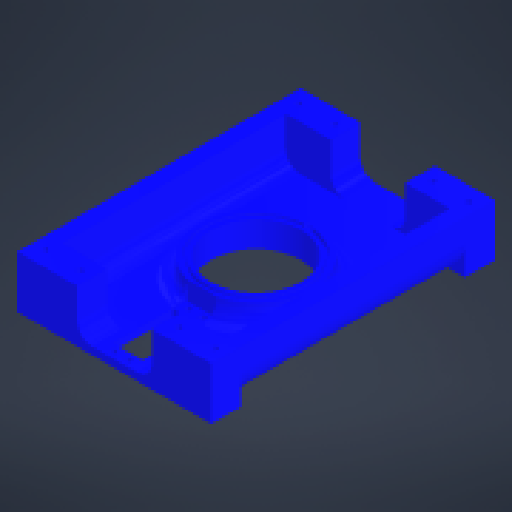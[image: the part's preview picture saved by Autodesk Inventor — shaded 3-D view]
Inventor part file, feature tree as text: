
AUTODESK INVENTOR PART (.ipt)
format: ipt  version: 2024 (Build 280153000, 153)  size: 495,616 bytes
history: native  units: mm
features: other x11, reference x9, extrude x8, sketch x8, projected_geometry x3, mirror x2, imported_body x1
ambient origin geometry x8: Origin, YZ Plane, XZ Plane, XY Plane, X Axis, Y Axis, Z Axis, Center Point
bodies: Body1 (feature_tree)
feature tree (42):
  other  "Твердое тело1"
  extrude  "Выдавливание2"  TaperAngle=0.0deg  [1 undecoded]
  other  "РабПлоскость1"
  other  "РабПлоскость2"
  mirror  "Зеркальное отражение1"
  mirror  "Зеркальное отражение2"
  extrude  "Выдавливание1"  Depth=20.0mm TaperAngle=0.0deg
  extrude  "Выдавливание3"  Depth=2.0mm
  extrude  "Выдавливание4"  Depth=60.5mm
  extrude  "Выдавливание5"  Depth=38.0mm
  extrude  "Выдавливание6"  Depth=2.875mm
  extrude  "Выдавливание7"  Depth=3.0mm TaperAngle=0.0deg
  extrude  "Выдавливание8"  Depth=3.0mm TaperAngle=0.0deg
  sketch  "Эскиз1"
  reference  "Ссылка1"
  reference  "Ссылка2"
  reference  "Ссылка3"
  reference  "Ссылка4"
  reference  "Ссылка5"
  reference  "Ссылка6"
  reference  "Ссылка7"
  reference  "Ссылка8"
  sketch  "Эскиз2"
  sketch  "Эскиз3"
  sketch  "Эскиз4"
  projected_geometry  "Спроецированная петля1"
  sketch  "Эскиз5"
  sketch  "Эскиз6"
  sketch  "Эскиз7"
  projected_geometry  "Спроецированная петля2"
  projected_geometry  "Спроецированная петля3"
  sketch  "Эскиз8"
  reference  "Ссылка9"
  imported_body  "БазТело1"
  parser-record x2  (decoder bookkeeping rows leaked as tree rows — omitted from the tree; the rows remain in map.json)
  other  "main_assembly.iam"
  other  "base_assambly:1"
  other  "side_axis:2"
  other  "side_axis:1"
  other  "manipulator.iam"
  other  "servo_40kg:1"
note: 1 required parameter value undecoded (feature->parameter linkage not recoverable at this tier; creation-order binding heuristic only, values carry confidence <= 0.55)
note: 2 file-system paths scrubbed to <path> (originals preserved in map.json)
